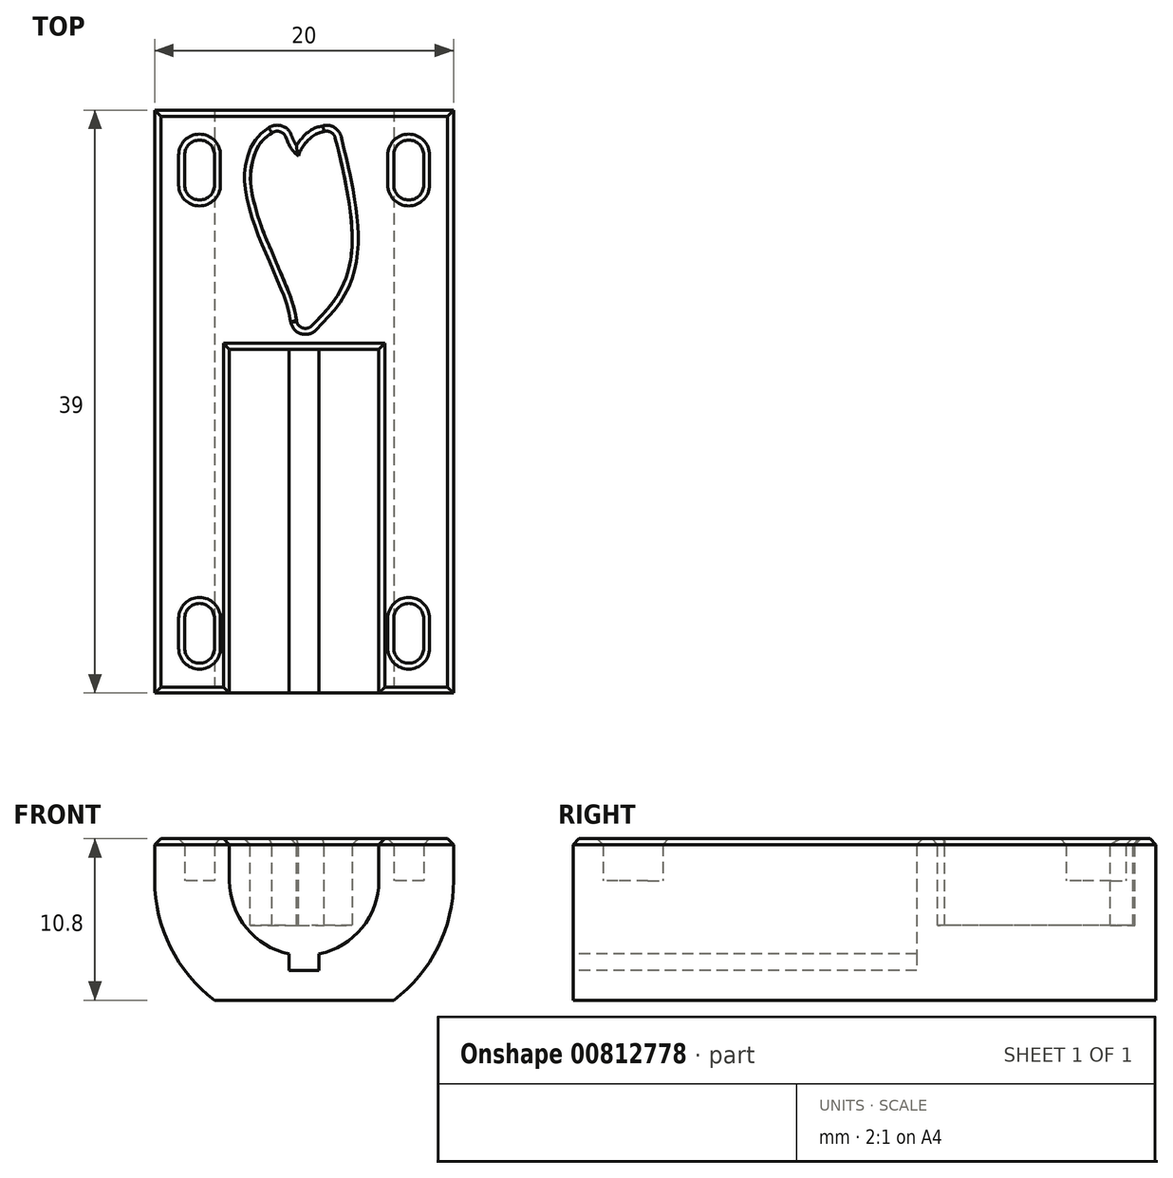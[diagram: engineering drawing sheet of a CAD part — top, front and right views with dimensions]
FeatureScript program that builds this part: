
annotation { "Feature Type Name" : "Feature", "Feature Type Description" : "" }
export const myFeature = defineFeature(function(context is Context, id is Id, definition is map)
    precondition{}
    {
        {
            var Q0;
            Q0=qCreatedBy(makeId("Top.planeOp"),FACE);
            var sketch = newSketch(context, id + "F0", { "sketchPlane" : qUnion([Q0])});
            skLineSegment(sketch, "E0", {"start": v(0, 41.82) * mm, "end": v(0, -8.8) * mm, "construction": true});
            skSolve(sketch);
        }
        {
            var Q0;
            Q0=qCreatedBy(makeId("Top.planeOp"),FACE);
            var sketch = newSketch(context, id + "F1", { "sketchPlane" : qUnion([Q0])});
            skLineSegment(sketch, "E1.bottom", {"start": v(-10, 39) * mm, "end": v(10, 39) * mm});
            skLineSegment(sketch, "E1.top", {"start": v(-10, 0) * mm, "end": v(10, 0) * mm});
            skLineSegment(sketch, "E1.left", {"start": v(-10, 39) * mm, "end": v(-10, 0) * mm});
            skLineSegment(sketch, "E1.right", {"start": v(10, 39) * mm, "end": v(10, 0) * mm});
            skSolve(sketch);
        }
        {
            var Q0;
            Q0=makeQuery(id+"F1.imprint","IMPRINT",FACE,{"disambiguationData":[TD([[makeQuery(id+"F1.imprint","IMPRINT",EDGE,{"derivedFrom":sQuery(id+"F1.wireOp",EDGE,"E1.bottom")}),-1.0]])]});
            extrude(context, id + "F2", {"entities" : qUnion([Q0]), "oppositeDirection" : true, "depth" : 8 * mm, "offsetDistance" : 25 * mm});
        }
        {
            var Q0;
            Q0=makeQuery(id+"F2.opExtrude","SWEPT_FACE",FACE,{"disambiguationData":[OSD([sQuery(id+"F1.wireOp",EDGE,"E1.top")])]});
            var sketch = newSketch(context, id + "F3", { "sketchPlane" : qUnion([Q0])});
            skCircle(sketch, "E2", {"center": v(0, 0) * mm, "radius": 5 * mm});
            skSolve(sketch);
        }
        {
            var Q0;
            {var subQ0=sQuery(id+"F3.wireOp",EDGE,"E2");var subQ1=makeQuery(id+"F2.opExtrude","CAP_EDGE",EDGE,{"disambiguationData":[OSD([sQuery(id+"F1.wireOp",EDGE,"E1.top")])],"isStart":true});var subQ2=makeQuery(id+"F3.imprint","INTERSECT",VERTEX,{"disambiguationData":[OD(0.0)],"derivedFrom":[subQ1,subQ0]});Q0=makeQuery(id+"F3.imprint","IMPRINT",FACE,{"disambiguationData":[TD([[makeQuery(id+"F3.imprint","IMPRINT",EDGE,{"disambiguationData":[TD([[subQ2,-1.0]])],"derivedFrom":subQ0}),1.0]])]});}
            extrude(context, id + "F4", {"entities" : qUnion([Q0]), "operationType" : NewBodyOperationType.REMOVE, "oppositeDirection" : true, "depth" : 23 * mm, "offsetDistance" : 25 * mm});
        }
        {
            var Q0;
            Q0=makeQuery(id+"F2.opExtrude","CAP_FACE",FACE,{"disambiguationData":[OSD([sQuery(id+"F1.wireOp",EDGE,"E1.bottom"),sQuery(id+"F1.wireOp",EDGE,"E1.top"),sQuery(id+"F1.wireOp",EDGE,"E1.left"),sQuery(id+"F1.wireOp",EDGE,"E1.right")])],"isStart":true});
            var sketch = newSketch(context, id + "F5", { "sketchPlane" : qUnion([Q0])});
            skLineSegment(sketch, "E3", {"start": v(-5, 23) * mm, "end": v(-5, 39) * mm, "construction": true});
            skLineSegment(sketch, "E4", {"start": v(5, 23) * mm, "end": v(5, 39) * mm, "construction": true});
            skLineSegment(sketch, "E5", {"start": v(-5, 25) * mm, "end": v(5.17, 25) * mm, "construction": true});
            skCircle(sketch, "E6", {"center": v(0.09, 25) * mm, "radius": 0.6 * mm, "construction": true});
            skLineSegment(sketch, "E7", {"start": v(-5, 35) * mm, "end": v(5, 35) * mm, "construction": true});
            skLineSegment(sketch, "E8", {"start": v(-5, 37) * mm, "end": v(5, 37) * mm, "construction": true});
            skCircle(sketch, "E9", {"center": v(0, 35) * mm, "radius": 0.6 * mm, "construction": true});
            skCircle(sketch, "E10", {"center": v(1.5, 37) * mm, "radius": 0.6 * mm, "construction": true});
            skCircle(sketch, "E11", {"center": v(-1.8, 37) * mm, "radius": 0.6 * mm, "construction": true});
            skFitSpline(sketch, "E12", {"points": [v(-1.8, 37) * mm, v(-2.81, 33.22) * mm, v(0.09, 25) * mm], "startDerivative": vector(-8.26, -6) * mm, "endDerivative": vector(3, -13.97) * mm});
            skFitSpline(sketch, "E13", {"points": [v(0, 35) * mm, v(0.38, 36.14) * mm, v(1.5, 37) * mm], "startDerivative": vector(0.69, 2.9) * mm, "endDerivative": vector(3.32, 0.95) * mm});
            skFitSpline(sketch, "E14", {"points": [v(1.5, 37) * mm, v(2.25, 28.04) * mm, v(0.09, 25) * mm], "startDerivative": vector(6.59, -26.82) * mm, "endDerivative": vector(-9.9, -10.3) * mm});
            skFitSpline(sketch, "E15", {"points": [v(-1.8, 37) * mm, v(-1.13, 35.82) * mm, v(0, 35) * mm], "startDerivative": vector(2.01, -4.95) * mm, "endDerivative": vector(4.8, -2.73) * mm});
            skArc(sketch, "E16.0.startCap", {"start": v(-2.36, 36.77) * mm, "mid": v(-2.03, 37.56) * mm, "end": v(-1.24, 37.23) * mm});
            skArc(sketch, "E16.0.endCap", {"start": v(0.3, 35.52) * mm, "mid": v(0.52, 34.7) * mm, "end": v(-0.3, 34.48) * mm});
            skFitSpline(sketch, "E16.0.left", {"points": [v(-1.24, 37.23) * mm, v(-1.16, 37.03) * mm, v(-1.03, 36.72) * mm, v(-0.9, 36.5) * mm, v(-0.83, 36.4) * mm, v(-0.79, 36.33) * mm, v(-0.75, 36.29) * mm, v(-0.72, 36.25) * mm, v(-0.68, 36.2) * mm, v(-0.63, 36.16) * mm, v(-0.58, 36.1) * mm, v(-0.52, 36.05) * mm, v(-0.42, 35.97) * mm, v(-0.2, 35.81) * mm, v(0.1, 35.63) * mm, v(0.3, 35.52) * mm]});
            skFitSpline(sketch, "E16.0.right", {"points": [v(-2.36, 36.77) * mm, v(-2.27, 36.56) * mm, v(-2.11, 36.2) * mm, v(-1.94, 35.9) * mm, v(-1.82, 35.7) * mm, v(-1.72, 35.58) * mm, v(-1.65, 35.5) * mm, v(-1.6, 35.44) * mm, v(-1.56, 35.4) * mm, v(-1.5, 35.33) * mm, v(-1.41, 35.24) * mm, v(-1.3, 35.14) * mm, v(-1.13, 35) * mm, v(-0.84, 34.8) * mm, v(-0.5, 34.6) * mm, v(-0.3, 34.48) * mm]});
            skArc(sketch, "E16.1.startCap", {"start": v(-2.15, 37.49) * mm, "mid": v(-1.31, 37.35) * mm, "end": v(-1.45, 36.51) * mm});
            skArc(sketch, "E16.1.endCap", {"start": v(0.67, 25.13) * mm, "mid": v(0.21, 24.41) * mm, "end": v(-0.5, 24.87) * mm});
            skFitSpline(sketch, "E16.1.left", {"points": [v(-1.45, 36.51) * mm, v(-1.72, 36.32) * mm, v(-2.01, 35.97) * mm, v(-2.25, 35.39) * mm, v(-2.38, 34.7) * mm, v(-2.34, 33.88) * mm, v(-2.14, 32.94) * mm, v(-1.83, 31.92) * mm, v(-1.3, 30.55) * mm, v(-0.55, 28.79) * mm, v(0.17, 26.97) * mm, v(0.54, 25.74) * mm, v(0.67, 25.13) * mm]});
            skFitSpline(sketch, "E16.1.right", {"points": [v(-2.15, 37.49) * mm, v(-2.57, 37.18) * mm, v(-3.06, 36.62) * mm, v(-3.41, 35.72) * mm, v(-3.6, 34.75) * mm, v(-3.54, 33.71) * mm, v(-3.3, 32.63) * mm, v(-2.96, 31.51) * mm, v(-2.4, 30.08) * mm, v(-1.4, 27.74) * mm, v(-0.74, 25.97) * mm, v(-0.5, 24.87) * mm]});
            skArc(sketch, "E16.2.startCap", {"start": v(0.58, 34.86) * mm, "mid": v(-0.14, 34.42) * mm, "end": v(-0.58, 35.14) * mm});
            skArc(sketch, "E16.2.endCap", {"start": v(1.34, 37.58) * mm, "mid": v(2.08, 37.16) * mm, "end": v(1.66, 36.42) * mm});
            skFitSpline(sketch, "E16.2.left", {"points": [v(-0.58, 35.14) * mm, v(-0.53, 35.38) * mm, v(-0.43, 35.82) * mm, v(-0.2, 36.38) * mm, v(0.12, 36.83) * mm, v(0.54, 37.24) * mm, v(0.99, 37.48) * mm, v(1.34, 37.58) * mm]});
            skFitSpline(sketch, "E16.2.right", {"points": [v(0.58, 34.86) * mm, v(0.64, 35.1) * mm, v(0.71, 35.4) * mm, v(0.81, 35.69) * mm, v(0.9, 35.87) * mm, v(1.03, 36.04) * mm, v(1.24, 36.24) * mm, v(1.46, 36.36) * mm, v(1.66, 36.42) * mm]});
            skArc(sketch, "E16.3.startCap", {"start": v(0.92, 36.86) * mm, "mid": v(1.36, 37.58) * mm, "end": v(2.08, 37.14) * mm});
            skArc(sketch, "E16.3.endCap", {"start": v(0.52, 24.58) * mm, "mid": v(-0.33, 24.57) * mm, "end": v(-0.35, 25.42) * mm});
            skFitSpline(sketch, "E16.3.left", {"points": [v(2.08, 37.14) * mm, v(2.36, 36.02) * mm, v(2.8, 34.05) * mm, v(3.14, 31.8) * mm, v(3.22, 30.37) * mm, v(3.16, 29.42) * mm, v(3.07, 28.78) * mm, v(2.94, 28.21) * mm, v(2.77, 27.7) * mm, v(2.56, 27.22) * mm, v(2.21, 26.58) * mm, v(1.63, 25.77) * mm, v(0.94, 25.02) * mm, v(0.52, 24.58) * mm]});
            skFitSpline(sketch, "E16.3.right", {"points": [v(0.92, 36.86) * mm, v(1.19, 35.75) * mm, v(1.62, 33.82) * mm, v(1.95, 31.66) * mm, v(2.03, 30.1) * mm, v(1.93, 29.16) * mm, v(1.78, 28.55) * mm, v(1.64, 28.12) * mm, v(1.48, 27.74) * mm, v(1.2, 27.24) * mm, v(0.71, 26.55) * mm, v(0.06, 25.84) * mm, v(-0.35, 25.42) * mm]});
            skLineSegment(sketch, "E17", {"start": v(-4, 23) * mm, "end": v(-4, 39) * mm, "construction": true});
            skLineSegment(sketch, "E18", {"start": v(4, 23) * mm, "end": v(4, 39) * mm, "construction": true});
            skSolve(sketch);
        }
        {
            var Q0;
            {var subQ2=sQuery(id+"F5.wireOp",EDGE,"E16.0.startCap");Q0=makeQuery(id+"F5.imprint","IMPRINT",FACE,{"disambiguationData":[TD([[makeQuery(id+"F5.imprint","IMPRINT",EDGE,{"derivedFrom":subQ2}),1.0]])]});}
            var Q1;
            {var subQ1=sQuery(id+"F5.wireOp",EDGE,"E16.0.startCap");Q1=makeQuery(id+"F5.imprint","IMPRINT",FACE,{"disambiguationData":[TD([[makeQuery(id+"F5.imprint","IMPRINT",EDGE,{"derivedFrom":subQ1}),-1.0]])]});}
            var Q2;
            {var subQ3=sQuery(id+"F5.wireOp",EDGE,"E15");var subQ5=sQuery(id+"F5.wireOp",EDGE,"E12");var subQ6=makeQuery(id+"F5.imprint","INTERSECT",VERTEX,{"derivedFrom":[subQ5,subQ3]});Q2=makeQuery(id+"F5.imprint","IMPRINT",FACE,{"disambiguationData":[TD([[makeQuery(id+"F5.imprint","IMPRINT",EDGE,{"disambiguationData":[TD([[subQ6,-1.0]])],"derivedFrom":subQ5}),1.0]])]});}
            var Q3;
            {var subQ0=sQuery(id+"F5.wireOp",EDGE,"E16.0.right");var subQ1=sQuery(id+"F5.wireOp",EDGE,"E12");var subQ2=makeQuery(id+"F5.imprint","INTERSECT",VERTEX,{"derivedFrom":[subQ1,subQ0]});Q3=makeQuery(id+"F5.imprint","IMPRINT",FACE,{"disambiguationData":[TD([[makeQuery(id+"F5.imprint","IMPRINT",EDGE,{"disambiguationData":[TD([[subQ2,-1.0]])],"derivedFrom":subQ1}),1.0]])]});}
            var Q4;
            {var subQ1=sQuery(id+"F5.wireOp",EDGE,"E16.1.startCap");var subQ3=sQuery(id+"F5.wireOp",EDGE,"E15");var subQ4=makeQuery(id+"F5.imprint","INTERSECT",VERTEX,{"derivedFrom":[subQ3,subQ1]});Q4=makeQuery(id+"F5.imprint","IMPRINT",FACE,{"disambiguationData":[TD([[makeQuery(id+"F5.imprint","IMPRINT",EDGE,{"disambiguationData":[TD([[subQ4,-1.0]])],"derivedFrom":subQ3}),-1.0]])]});}
            var Q5;
            {var subQ0=sQuery(id+"F5.wireOp",EDGE,"E16.1.startCap");var subQ1=sQuery(id+"F5.wireOp",EDGE,"E15");var subQ2=makeQuery(id+"F5.imprint","INTERSECT",VERTEX,{"derivedFrom":[subQ1,subQ0]});Q5=makeQuery(id+"F5.imprint","IMPRINT",FACE,{"disambiguationData":[TD([[makeQuery(id+"F5.imprint","IMPRINT",EDGE,{"disambiguationData":[TD([[subQ2,-1.0]])],"derivedFrom":subQ1}),1.0]])]});}
            var Q6;
            {var subQ0=sQuery(id+"F5.wireOp",EDGE,"E15");var subQ1=sQuery(id+"F5.wireOp",EDGE,"E13");var subQ2=makeQuery(id+"F5.imprint","INTERSECT",VERTEX,{"derivedFrom":[subQ1,subQ0]});Q6=makeQuery(id+"F5.imprint","IMPRINT",FACE,{"disambiguationData":[TD([[makeQuery(id+"F5.imprint","IMPRINT",EDGE,{"disambiguationData":[TD([[subQ2,-1.0]])],"derivedFrom":subQ1}),1.0]])]});}
            var Q7;
            {var subQ1=sQuery(id+"F5.wireOp",EDGE,"E16.0.endCap");Q7=makeQuery(id+"F5.imprint","IMPRINT",FACE,{"disambiguationData":[TD([[makeQuery(id+"F5.imprint","IMPRINT",EDGE,{"derivedFrom":subQ1}),-1.0]])]});}
            var Q8;
            {var subQ1=sQuery(id+"F5.wireOp",EDGE,"E16.0.endCap");Q8=makeQuery(id+"F5.imprint","IMPRINT",FACE,{"disambiguationData":[TD([[makeQuery(id+"F5.imprint","IMPRINT",EDGE,{"derivedFrom":subQ1}),1.0]])]});}
            var Q9;
            {var subQ5=sQuery(id+"F5.wireOp",EDGE,"E16.0.left");var subQ6=sQuery(id+"F5.wireOp",EDGE,"E13");var subQ7=makeQuery(id+"F5.imprint","INTERSECT",VERTEX,{"derivedFrom":[subQ6,subQ5]});Q9=makeQuery(id+"F5.imprint","IMPRINT",FACE,{"disambiguationData":[TD([[makeQuery(id+"F5.imprint","IMPRINT",EDGE,{"disambiguationData":[TD([[subQ7,-1.0]])],"derivedFrom":subQ6}),1.0]])]});}
            var Q10;
            {var subQ1=sQuery(id+"F5.wireOp",EDGE,"E16.2.endCap");Q10=makeQuery(id+"F5.imprint","IMPRINT",FACE,{"disambiguationData":[TD([[makeQuery(id+"F5.imprint","IMPRINT",EDGE,{"derivedFrom":subQ1}),-1.0]])]});}
            var Q11;
            {var subQ0=sQuery(id+"F5.wireOp",EDGE,"E14");var subQ1=sQuery(id+"F5.wireOp",EDGE,"E13");var subQ2=makeQuery(id+"F5.imprint","INTERSECT",VERTEX,{"derivedFrom":[subQ1,subQ0]});Q11=makeQuery(id+"F5.imprint","IMPRINT",FACE,{"disambiguationData":[TD([[makeQuery(id+"F5.imprint","IMPRINT",EDGE,{"disambiguationData":[TD([[subQ2,1.0]])],"derivedFrom":subQ1}),-1.0]])]});}
            var Q12;
            {var subQ0=sQuery(id+"F5.wireOp",EDGE,"E16.2.right");var subQ1=sQuery(id+"F5.wireOp",EDGE,"E14");var subQ2=makeQuery(id+"F5.imprint","INTERSECT",VERTEX,{"derivedFrom":[subQ1,subQ0]});Q12=makeQuery(id+"F5.imprint","IMPRINT",FACE,{"disambiguationData":[TD([[makeQuery(id+"F5.imprint","IMPRINT",EDGE,{"disambiguationData":[TD([[subQ2,-1.0]])],"derivedFrom":subQ1}),-1.0]])]});}
            var Q13;
            {var subQ1=sQuery(id+"F5.wireOp",EDGE,"E16.1.endCap");Q13=makeQuery(id+"F5.imprint","IMPRINT",FACE,{"disambiguationData":[TD([[makeQuery(id+"F5.imprint","IMPRINT",EDGE,{"derivedFrom":subQ1}),1.0]])]});}
            var Q14;
            {var subQ0=sQuery(id+"F5.wireOp",EDGE,"E14");var subQ1=sQuery(id+"F5.wireOp",EDGE,"E12");var subQ2=makeQuery(id+"F5.imprint","INTERSECT",VERTEX,{"derivedFrom":[subQ1,subQ0]});Q14=makeQuery(id+"F5.imprint","IMPRINT",FACE,{"disambiguationData":[TD([[makeQuery(id+"F5.imprint","IMPRINT",EDGE,{"disambiguationData":[TD([[subQ2,1.0]])],"derivedFrom":subQ1}),1.0]])]});}
            var Q15;
            {var subQ0=sQuery(id+"F5.wireOp",EDGE,"E16.1.endCap");Q15=makeQuery(id+"F5.imprint","IMPRINT",FACE,{"disambiguationData":[TD([[makeQuery(id+"F5.imprint","IMPRINT",EDGE,{"derivedFrom":subQ0}),-1.0]])]});}
            var Q16;
            {var subQ0=sQuery(id+"F5.wireOp",EDGE,"E16.1.left");var subQ1=sQuery(id+"F5.wireOp",EDGE,"E15");var subQ2=makeQuery(id+"F5.imprint","INTERSECT",VERTEX,{"derivedFrom":[subQ1,subQ0]});Q16=makeQuery(id+"F5.imprint","IMPRINT",FACE,{"disambiguationData":[TD([[makeQuery(id+"F5.imprint","IMPRINT",EDGE,{"disambiguationData":[TD([[subQ2,-1.0]])],"derivedFrom":subQ1}),-1.0]])]});}
            var Q17;
            {var subQ0=sQuery(id+"F5.wireOp",EDGE,"E16.1.left");var subQ3=sQuery(id+"F5.wireOp",EDGE,"E15");var subQ4=makeQuery(id+"F5.imprint","INTERSECT",VERTEX,{"derivedFrom":[subQ3,subQ0]});Q17=makeQuery(id+"F5.imprint","IMPRINT",FACE,{"disambiguationData":[TD([[makeQuery(id+"F5.imprint","IMPRINT",EDGE,{"disambiguationData":[TD([[subQ4,-1.0]])],"derivedFrom":subQ3}),1.0]])]});}
            var Q18;
            {var subQ4=sQuery(id+"F5.wireOp",EDGE,"E14");var subQ5=sQuery(id+"F5.wireOp",EDGE,"E13");var subQ6=makeQuery(id+"F5.imprint","INTERSECT",VERTEX,{"derivedFrom":[subQ5,subQ4]});Q18=makeQuery(id+"F5.imprint","IMPRINT",FACE,{"disambiguationData":[TD([[makeQuery(id+"F5.imprint","IMPRINT",EDGE,{"disambiguationData":[TD([[subQ6,1.0]])],"derivedFrom":subQ5}),1.0]])]});}
            var Q19;
            {var subQ1=sQuery(id+"F5.wireOp",EDGE,"E14");var subQ6=sQuery(id+"F5.wireOp",EDGE,"E16.2.endCap");var subQ9=makeQuery(id+"F5.imprint","INTERSECT",VERTEX,{"derivedFrom":[subQ1,subQ6]});Q19=makeQuery(id+"F5.imprint","IMPRINT",FACE,{"disambiguationData":[TD([[makeQuery(id+"F5.imprint","IMPRINT",EDGE,{"disambiguationData":[TD([[subQ9,-1.0]])],"derivedFrom":subQ1}),-1.0]])]});}
            extrude(context, id + "F6", {"entities" : qUnion([Q0, Q1, Q2, Q3, Q4, Q5, Q6, Q7, Q8, Q9, Q10, Q11, Q12, Q13, Q14, Q15, Q16, Q17, Q18, Q19]), "operationType" : NewBodyOperationType.REMOVE, "oppositeDirection" : true, "depth" : 3 * mm, "offsetDistance" : 25 * mm});
        }
        {
            var Q0;
            Q0=qCreatedBy(makeId("Top.planeOp"),FACE);
            cPlane(context, id + "F7", {"entities" : qUnion([Q0]), "cplaneType" : CPlaneType.OFFSET, "offset" : 6 * mm, "oppositeDirection" : true, "width" : 150 * mm, "height" : 150 * mm});
        }
        {
            var Q0;
            Q0=qCreatedBy(id+"F7.planeOp",FACE);
            var sketch = newSketch(context, id + "F8", { "sketchPlane" : qUnion([Q0])});
            skLineSegment(sketch, "E19.bottom", {"start": v(-1, 23) * mm, "end": v(1, 23) * mm});
            skLineSegment(sketch, "E19.top", {"start": v(-1, 0) * mm, "end": v(1, 0) * mm});
            skLineSegment(sketch, "E19.left", {"start": v(-1, 23) * mm, "end": v(-1, 0) * mm});
            skLineSegment(sketch, "E19.right", {"start": v(1, 23) * mm, "end": v(1, 0) * mm});
            skSolve(sketch);
        }
        {
            var Q0;
            Q0=makeQuery(id+"F8.imprint","IMPRINT",FACE,{"disambiguationData":[TD([[makeQuery(id+"F8.imprint","IMPRINT",EDGE,{"derivedFrom":sQuery(id+"F8.wireOp",EDGE,"E19.bottom")}),-1.0]])]});
            extrude(context, id + "F9", {"entities" : qUnion([Q0]), "operationType" : NewBodyOperationType.REMOVE, "endBound" : BoundingType.THROUGH_ALL, "depth" : 2 * mm, "offsetDistance" : 25 * mm});
        }
        {
            var Q0;
            Q0=makeQuery(id+"F2.opExtrude","SWEPT_FACE",FACE,{"disambiguationData":[OSD([sQuery(id+"F1.wireOp",EDGE,"E1.top")])]});
            var sketch = newSketch(context, id + "F10", { "sketchPlane" : qUnion([Q0])});
            skCircle(sketch, "E20", {"center": v(0, 0) * mm, "radius": 10 * mm});
            skLineSegment(sketch, "E21", {"start": v(-10, 0) * mm, "end": v(-10, -8) * mm});
            skLineSegment(sketch, "E22", {"start": v(-10, -8) * mm, "end": v(-6, -8) * mm});
            skLineSegment(sketch, "E23", {"start": v(6, -8) * mm, "end": v(10, -8) * mm});
            skLineSegment(sketch, "E24", {"start": v(10, -8) * mm, "end": v(10, 0) * mm});
            skSolve(sketch);
        }
        {
            var Q0;
            {var subQ0=sQuery(id+"F10.wireOp",EDGE,"E21");Q0=makeQuery(id+"F10.imprint","IMPRINT",FACE,{"disambiguationData":[TD([[makeQuery(id+"F10.imprint","IMPRINT",EDGE,{"derivedFrom":subQ0}),-1.0]])]});}
            var Q1;
            {var subQ4=sQuery(id+"F10.wireOp",EDGE,"E23");Q1=makeQuery(id+"F10.imprint","IMPRINT",FACE,{"disambiguationData":[TD([[makeQuery(id+"F10.imprint","IMPRINT",EDGE,{"derivedFrom":subQ4}),1.0]])]});}
            extrude(context, id + "F11", {"entities" : qUnion([Q0, Q1]), "operationType" : NewBodyOperationType.REMOVE, "endBound" : BoundingType.THROUGH_ALL, "oppositeDirection" : true, "depth" : 25 * mm, "offsetDistance" : 25 * mm});
        }
        {
            var Q0;
            {var subQ0=sQuery(id+"F1.wireOp",EDGE,"E1.bottom");var subQ2=sQuery(id+"F1.wireOp",EDGE,"E1.top");var subQ3=sQuery(id+"F1.wireOp",EDGE,"E1.right");var subQ4=sQuery(id+"F1.wireOp",EDGE,"E1.left");Q0=makeQuery(id+"F6.boolean.opBoolean","SPLIT",FACE,{"disambiguationData":[TD([makeQuery(id+"F2.opExtrude","SWEPT_FACE",FACE,{"disambiguationData":[OSD([subQ0])]})])],"derivedFrom":makeQuery(id+"F2.opExtrude","CAP_FACE",FACE,{"disambiguationData":[OSD([subQ0,subQ2,subQ4,subQ3])],"isStart":true})});}
            var sketch = newSketch(context, id + "F12", { "sketchPlane" : qUnion([Q0])});
            skLineSegment(sketch, "E25", {"start": v(-7, 5) * mm, "end": v(-7, 3) * mm});
            skLineSegment(sketch, "E26", {"start": v(7, 5) * mm, "end": v(7, 3) * mm});
            skArc(sketch, "E27.0.startCap", {"start": v(-8, 5) * mm, "mid": v(-7, 6) * mm, "end": v(-6, 5) * mm});
            skArc(sketch, "E27.0.endCap", {"start": v(-6, 3) * mm, "mid": v(-7, 2) * mm, "end": v(-8, 3) * mm});
            skLineSegment(sketch, "E27.0.left", {"start": v(-6, 5) * mm, "end": v(-6, 3) * mm});
            skLineSegment(sketch, "E27.0.right", {"start": v(-8, 5) * mm, "end": v(-8, 3) * mm});
            skArc(sketch, "E28.0.startCap", {"start": v(6, 5) * mm, "mid": v(7, 6) * mm, "end": v(8, 5) * mm});
            skArc(sketch, "E28.0.endCap", {"start": v(8, 3) * mm, "mid": v(7, 2) * mm, "end": v(6, 3) * mm});
            skLineSegment(sketch, "E28.0.left", {"start": v(8, 5) * mm, "end": v(8, 3) * mm});
            skLineSegment(sketch, "E28.0.right", {"start": v(6, 5) * mm, "end": v(6, 3) * mm});
            skLineSegment(sketch, "E29", {"start": v(-7, 36) * mm, "end": v(-7, 34) * mm});
            skLineSegment(sketch, "E30", {"start": v(7, 36) * mm, "end": v(7, 34) * mm});
            skArc(sketch, "E31.0.startCap", {"start": v(-8, 36) * mm, "mid": v(-7, 37) * mm, "end": v(-6, 36) * mm});
            skArc(sketch, "E31.0.endCap", {"start": v(-6, 34) * mm, "mid": v(-7, 33) * mm, "end": v(-8, 34) * mm});
            skLineSegment(sketch, "E31.0.left", {"start": v(-6, 36) * mm, "end": v(-6, 34) * mm});
            skLineSegment(sketch, "E31.0.right", {"start": v(-8, 36) * mm, "end": v(-8, 34) * mm});
            skArc(sketch, "E32.0.startCap", {"start": v(6, 36) * mm, "mid": v(7, 37) * mm, "end": v(8, 36) * mm});
            skArc(sketch, "E32.0.endCap", {"start": v(8, 34) * mm, "mid": v(7, 33) * mm, "end": v(6, 34) * mm});
            skLineSegment(sketch, "E32.0.left", {"start": v(8, 36) * mm, "end": v(8, 34) * mm});
            skLineSegment(sketch, "E32.0.right", {"start": v(6, 36) * mm, "end": v(6, 34) * mm});
            skSolve(sketch);
        }
        {
            var Q0;
            Q0=makeQuery(id+"F12.imprint","IMPRINT",FACE,{"disambiguationData":[TD([[makeQuery(id+"F12.imprint","IMPRINT",EDGE,{"derivedFrom":sQuery(id+"F12.wireOp",EDGE,"E27.0.startCap")}),-1.0]])]});
            var Q1;
            Q1=makeQuery(id+"F12.imprint","IMPRINT",FACE,{"disambiguationData":[TD([[makeQuery(id+"F12.imprint","IMPRINT",EDGE,{"derivedFrom":sQuery(id+"F12.wireOp",EDGE,"E28.0.startCap")}),-1.0]])]});
            var Q2;
            Q2=makeQuery(id+"F12.imprint","IMPRINT",FACE,{"disambiguationData":[TD([[makeQuery(id+"F12.imprint","IMPRINT",EDGE,{"derivedFrom":sQuery(id+"F12.wireOp",EDGE,"E31.0.startCap")}),-1.0]])]});
            var Q3;
            Q3=makeQuery(id+"F12.imprint","IMPRINT",FACE,{"disambiguationData":[TD([[makeQuery(id+"F12.imprint","IMPRINT",EDGE,{"derivedFrom":sQuery(id+"F12.wireOp",EDGE,"E32.0.startCap")}),-1.0]])]});
            extrude(context, id + "F13", {"entities" : qUnion([Q0, Q1, Q2, Q3]), "operationType" : NewBodyOperationType.ADD, "depth" : 2.8 * mm, "offsetDistance" : 25 * mm});
        }
        {
            var Q0;
            Q0=makeQuery(id+"F13.opExtrude","CAP_FACE",FACE,{"disambiguationData":[OSD([sQuery(id+"F12.wireOp",EDGE,"E27.0.startCap"),sQuery(id+"F12.wireOp",EDGE,"E27.0.endCap"),sQuery(id+"F12.wireOp",EDGE,"E27.0.left"),sQuery(id+"F12.wireOp",EDGE,"E27.0.right")])],"isStart":false});
            var Q1;
            Q1=makeQuery(id+"F13.opExtrude","CAP_FACE",FACE,{"disambiguationData":[OSD([sQuery(id+"F12.wireOp",EDGE,"E28.0.startCap"),sQuery(id+"F12.wireOp",EDGE,"E28.0.endCap"),sQuery(id+"F12.wireOp",EDGE,"E28.0.left"),sQuery(id+"F12.wireOp",EDGE,"E28.0.right")])],"isStart":false});
            var Q2;
            Q2=makeQuery(id+"F13.opExtrude","CAP_FACE",FACE,{"disambiguationData":[OSD([sQuery(id+"F12.wireOp",EDGE,"E31.0.startCap"),sQuery(id+"F12.wireOp",EDGE,"E31.0.endCap"),sQuery(id+"F12.wireOp",EDGE,"E31.0.left"),sQuery(id+"F12.wireOp",EDGE,"E31.0.right")])],"isStart":false});
            var Q3;
            Q3=makeQuery(id+"F13.opExtrude","CAP_FACE",FACE,{"disambiguationData":[OSD([sQuery(id+"F12.wireOp",EDGE,"E32.0.startCap"),sQuery(id+"F12.wireOp",EDGE,"E32.0.endCap"),sQuery(id+"F12.wireOp",EDGE,"E32.0.left"),sQuery(id+"F12.wireOp",EDGE,"E32.0.right")])],"isStart":false});
            chamfer(context, id + "F14", {"entities" : qUnion([Q0, Q1, Q2, Q3]), "width" : .4 * mm, "tangentPropagation" : true});
        }
    });
